# Revit family: Flooring_Entrance-Flooring_emco_MARSCHALL-Original
name_source: partatom
category: Furniture Systems
revit_build: Autodesk Revit 2018 (Build: 20190510_1515(x64)
units: mm (PartAtom-declared; Revit-internal decimal feet)

## family parameters
Cut with Voids When Loaded = No
Host = Face
OmniClass Number = 23.15.17.11.11
OmniClass Title = Floor Toppings
Part Type = Normal
Room Calculation Point = No
Round Connector Dimension = Use Diameter
Shared = No

## types (27) — shared parameters
Assembly Code = E2010400
Date Updated = 2023/08/22
Default Elevation = 1219 mm
Description = Rollable and hard-wearing original entrance mat with standard insert for supported installation options.
Keynote = 12480.A1
Manufacturer = Emco
Product data url = https://bimobject.com
Profile Material = Emco - Metal - Aluminium
Standard profile clearance approx. (mm) = 5 mm, rubber spacers
URL = https://www.emco-bau.com
Version = 1

## per-type parameters (varying)
- Large With ribbed carpet insert 512 SLR: Brush strip=No; Cassette brush=No; Colour fastness to artificial light ISO 105-B02=good 6; Colour fastness to rubbing ISO 105 X12=good 4; Colour fastness to water ISO 105 E01=good 5; EPIMID=99871; Flammability=Insert available on request (surcharge applicable) with fire classification Cfl-s1 according to EN 13501.; Height 12=Yes; Height 17=No; Height 22=No; Large=Yes; Model=Large With ribbed carpet insert 512 SLR; Normal=No; Pile material=100% PP (polypropylene); Profile width (mm)=46.5 mm; Scraping edge=No; Slip resistance=R 11 slip resistance as per DIN 51130; Tread surface=Recessed, robust, weather-proof, ribbed carpet strips.; Weight (kg/m2)=95; z_Height=12 mm  [stored 0.0393701 ft]; z_edge_height=16 mm  [stored 0.0524934 ft]; z_insert_offset=52 mm; z_insert_width=47 mm; z_slot_offest=49 mm  [stored 0.160761 ft]; z_slot_width=5 mm  [stored 0.0164042 ft]
- Large With ribbed carpet insert 517 SLR: Brush strip=No; Cassette brush=No; Colour fastness to artificial light ISO 105-B02=good 6; Colour fastness to rubbing ISO 105 X12=good 4; Colour fastness to water ISO 105 E01=good 5; EPIMID=99873; Flammability=Insert available on request (surcharge applicable) with fire classification Cfl-s1 according to EN 13501.; Height 12=No; Height 17=Yes; Height 22=No; Large=Yes; Model=Large With ribbed carpet insert 517 SLR; Normal=No; Pile material=100% PP (polypropylene); Profile width (mm)=46.5 mm; Scraping edge=No; Slip resistance=R 11 slip resistance as per DIN 51130; Tread surface=Recessed, robust, weather-proof, ribbed carpet strips.; Weight (kg/m2)=119; z_Height=17 mm; z_edge_height=20 mm  [stored 0.0656168 ft]; z_insert_offset=52 mm; z_insert_width=47 mm; z_slot_offest=49 mm  [stored 0.160761 ft]; z_slot_width=5 mm  [stored 0.0164042 ft]
- Large With ribbed carpet insert 522 SLR: Brush strip=No; Cassette brush=No; Colour fastness to artificial light ISO 105-B02=good 6; Colour fastness to rubbing ISO 105 X12=good 4; Colour fastness to water ISO 105 E01=good 5; EPIMID=99875; Flammability=Insert available on request (surcharge applicable) with fire classification Cfl-s1 according to EN 13501.; Height 12=No; Height 17=No; Height 22=Yes; Large=Yes; Model=Large With ribbed carpet insert 522 SLR; Normal=No; Pile material=100% PP (polypropylene); Profile width (mm)=46.5 mm; Scraping edge=No; Slip resistance=R 11 slip resistance as per DIN 51130; Tread surface=Recessed, robust, weather-proof, ribbed carpet strips.; Weight (kg/m2)=13.2; z_Height=22 mm  [stored 0.0721785 ft]; z_edge_height=25 mm  [stored 0.082021 ft]; z_insert_offset=52 mm; z_insert_width=47 mm; z_slot_offest=49 mm  [stored 0.160761 ft]; z_slot_width=5 mm  [stored 0.0164042 ft]
- Large With ribbed carpet insert and brush strip 517 SLRB: Brush strip=Yes; Cassette brush=No; Colour fastness to artificial light ISO 105-B02=good 6; Colour fastness to rubbing ISO 105 X12=good 4; Colour fastness to water ISO 105 E01=good 5; EPIMID=99939; Flammability=Insert available on request (surcharge applicable) with fire classification Cfl-s1 according to EN 13501.; Height 12=No; Height 17=Yes; Height 22=No; Large=Yes; Model=Large With ribbed carpet insert and brush strip 517 SLRB; Normal=No; Pile material=100% PP (polypropylene); Profile width (mm)=46.5 mm; Scraping edge=No; Slip resistance=-; Tread surface=Recessed, robust, weather-proof, ribbed carpet strips, also with brush strips mounted between the profiles.; Weight (kg/m2)=121; z_Height=17 mm; z_edge_height=20 mm  [stored 0.0656168 ft]; z_insert_offset=66 mm; z_insert_width=47 mm; z_slot_offest=56 mm; z_slot_width=20 mm  [stored 0.0656168 ft]
- Large With ribbed carpet insert and brush strip 522 SLRB: Brush strip=Yes; Cassette brush=No; Colour fastness to artificial light ISO 105-B02=good 6; Colour fastness to rubbing ISO 105 X12=good 4; Colour fastness to water ISO 105 E01=good 5; EPIMID=99941; Flammability=Insert available on request (surcharge applicable) with fire classification Cfl-s1 according to EN 13501.; Height 12=No; Height 17=No; Height 22=Yes; Large=Yes; Model=Large With ribbed carpet insert and brush strip 522 SLRB; Normal=No; Pile material=100% PP (polypropylene); Profile width (mm)=46.5 mm; Scraping edge=No; Slip resistance=-; Tread surface=Recessed, robust, weather-proof, ribbed carpet strips, also with brush strips mounted between the profiles.; Weight (kg/m2)=13.4; z_Height=22 mm  [stored 0.0721785 ft]; z_edge_height=25 mm  [stored 0.082021 ft]; z_insert_offset=66 mm; z_insert_width=47 mm; z_slot_offest=56 mm; z_slot_width=20 mm  [stored 0.0656168 ft]
- Large With ribbed carpet insert and scraper bar 512 SLRK: Brush strip=No; Cassette brush=No; Colour fastness to artificial light ISO 105-B02=good 6; Colour fastness to rubbing ISO 105 X12=good 4; Colour fastness to water ISO 105 E01=good 5; EPIMID=99944; Flammability=Insert available on request (surcharge applicable) with fire classification Cfl-s1 according to EN 13501.; Height 12=Yes; Height 17=No; Height 22=No; Large=Yes; Model=Large With ribbed carpet insert and scraper bar 512 SLRK; Normal=No; Pile material=100% PP (polypropylene); Profile width (mm)=46.5 mm; Scraping edge=Yes; Slip resistance=-; Tread surface=Recessed, robust, weather-proof, ribbed carpet strips, also with scraper bars mounted between the profiles.; Weight (kg/m2)=95; z_Height=12 mm  [stored 0.0393701 ft]; z_edge_height=16 mm  [stored 0.0524934 ft]; z_insert_offset=62 mm; z_insert_width=47 mm; z_slot_offest=54 mm; z_slot_width=15 mm  [stored 0.0492126 ft]
- Large With ribbed carpet insert and scraper bar 517 SLRK: Brush strip=No; Cassette brush=No; Colour fastness to artificial light ISO 105-B02=good 6; Colour fastness to rubbing ISO 105 X12=good 4; Colour fastness to water ISO 105 E01=good 5; EPIMID=99945; Flammability=Insert available on request (surcharge applicable) with fire classification Cfl-s1 according to EN 13501.; Height 12=No; Height 17=Yes; Height 22=No; Large=Yes; Model=Large With ribbed carpet insert and scraper bar 517 SLRK; Normal=No; Pile material=100% PP (polypropylene); Profile width (mm)=46.5 mm; Scraping edge=Yes; Slip resistance=-; Tread surface=Recessed, robust, weather-proof, ribbed carpet strips, also with scraper bars mounted between the profiles.; Weight (kg/m2)=12.3; z_Height=17 mm; z_edge_height=20 mm  [stored 0.0656168 ft]; z_insert_offset=62 mm; z_insert_width=47 mm; z_slot_offest=54 mm; z_slot_width=15 mm  [stored 0.0492126 ft]
- Large With ribbed carpet insert and scraper bar 522 SLRK: Brush strip=No; Cassette brush=No; Colour fastness to artificial light ISO 105-B02=good 6; Colour fastness to rubbing ISO 105 X12=good 4; Colour fastness to water ISO 105 E01=good 5; EPIMID=99947; Flammability=Insert available on request (surcharge applicable) with fire classification Cfl-s1 according to EN 13501.; Height 12=No; Height 17=No; Height 22=Yes; Large=Yes; Model=Large With ribbed carpet insert and scraper bar 522 SLRK; Normal=No; Pile material=100% PP (polypropylene); Profile width (mm)=46.5 mm; Scraping edge=Yes; Slip resistance=-; Tread surface=Recessed, robust, weather-proof, ribbed carpet strips, also with scraper bars mounted between the profiles.; Weight (kg/m2)=141; z_Height=22 mm  [stored 0.0721785 ft]; z_edge_height=25 mm  [stored 0.082021 ft]; z_insert_offset=62 mm; z_insert_width=47 mm; z_slot_offest=54 mm; z_slot_width=15 mm  [stored 0.0492126 ft]
- With cassette brush 512 SCB: Brush strip=No; Cassette brush=Yes; Colour fastness to artificial light ISO 105-B02=-; Colour fastness to rubbing ISO 105 X12=-; Colour fastness to water ISO 105 E01=-; EPIMID=99884; Flammability=Complete mat system (for bristle bundles in black) available on request (surcharge applicable) with fire classification Cfl-s1 according to EN 13501.; Height 12=Yes; Height 17=No; Height 22=No; Large=No; Model=With cassette brush 512 SCB; Normal=Yes; Pile material=-; Profile width (mm)=30 mm; Scraping edge=No; Slip resistance=R 13 slip resistance as per DIN 51130; Tread surface=Recessed, robust, weather-proof cassette sections, equipped with brush bundles arranged parallel to one another. Actual mat height: + 1 to 2 mm.; Weight (kg/m2)=167; z_Height=12 mm  [stored 0.0393701 ft]; z_edge_height=16 mm  [stored 0.0524934 ft]; z_insert_offset=35 mm; z_insert_width=30 mm  [stored 0.0984252 ft]; z_slot_offest=33 mm; z_slot_width=5 mm  [stored 0.0164042 ft]
- With cassette brush 517 SCB: Brush strip=No; Cassette brush=Yes; Colour fastness to artificial light ISO 105-B02=-; Colour fastness to rubbing ISO 105 X12=-; Colour fastness to water ISO 105 E01=-; EPIMID=99882; Flammability=Complete mat system (for bristle bundles in black) available on request (surcharge applicable) with fire classification Cfl-s1 according to EN 13501.; Height 12=No; Height 17=Yes; Height 22=No; Large=No; Model=With cassette brush 517 SCB; Normal=Yes; Pile material=-; Profile width (mm)=30 mm; Scraping edge=No; Slip resistance=R 13 slip resistance as per DIN 51130; Tread surface=Recessed, robust, weather-proof cassette sections, equipped with brush bundles arranged parallel to one another. Actual mat height: + 1 to 2 mm.; Weight (kg/m2)=194; z_Height=17 mm; z_edge_height=20 mm  [stored 0.0656168 ft]; z_insert_offset=35 mm; z_insert_width=30 mm  [stored 0.0984252 ft]; z_slot_offest=33 mm; z_slot_width=5 mm  [stored 0.0164042 ft]
- With cassette brush 522 SCB: Brush strip=No; Cassette brush=Yes; Colour fastness to artificial light ISO 105-B02=-; Colour fastness to rubbing ISO 105 X12=-; Colour fastness to water ISO 105 E01=-; EPIMID=99883; Flammability=Complete mat system (for bristle bundles in black) available on request (surcharge applicable) with fire classification Cfl-s1 according to EN 13501.; Height 12=No; Height 17=No; Height 22=Yes; Large=No; Model=With cassette brush 522 SCB; Normal=Yes; Pile material=-; Profile width (mm)=30 mm; Scraping edge=No; Slip resistance=R 13 slip resistance as per DIN 51130; Tread surface=Recessed, robust, weather-proof cassette sections, equipped with brush bundles arranged parallel to one another. Actual mat height: + 1 to 2 mm.; Weight (kg/m2)=215; z_Height=22 mm  [stored 0.0721785 ft]; z_edge_height=25 mm  [stored 0.082021 ft]; z_insert_offset=35 mm; z_insert_width=30 mm  [stored 0.0984252 ft]; z_slot_offest=33 mm; z_slot_width=5 mm  [stored 0.0164042 ft]
- With ribbed carpet insert 512 SR: Brush strip=No; Cassette brush=No; Colour fastness to artificial light ISO 105-B02=good 6; Colour fastness to rubbing ISO 105 X12=good 4; Colour fastness to water ISO 105 E01=good 5; EPIMID=99870; Flammability=Insert available on request (surcharge applicable) with fire classification Cfl-s1 according to EN 13501.; Height 12=Yes; Height 17=No; Height 22=No; Large=No; Model=With ribbed carpet insert 512 SR; Normal=Yes; Pile material=100% PP (polypropylene); Profile width (mm)=30 mm; Scraping edge=No; Slip resistance=R 11 slip resistance as per DIN 51130; Tread surface=Recessed, robust, weather-proof, ribbed carpet strips.; Weight (kg/m2)=11; z_Height=12 mm  [stored 0.0393701 ft]; z_edge_height=16 mm  [stored 0.0524934 ft]; z_insert_offset=35 mm; z_insert_width=30 mm  [stored 0.0984252 ft]; z_slot_offest=33 mm; z_slot_width=5 mm  [stored 0.0164042 ft]
- With ribbed carpet insert 517 SR: Brush strip=No; Cassette brush=No; Colour fastness to artificial light ISO 105-B02=good 6; Colour fastness to rubbing ISO 105 X12=good 4; Colour fastness to water ISO 105 E01=good 5; EPIMID=99872; Flammability=Insert available on request (surcharge applicable) with fire classification Cfl-s1 according to EN 13501.; Height 12=No; Height 17=Yes; Height 22=No; Large=No; Model=With ribbed carpet insert 517 SR; Normal=Yes; Pile material=100% PP (polypropylene); Profile width (mm)=30 mm; Scraping edge=No; Slip resistance=R 11 slip resistance as per DIN 51130; Tread surface=Recessed, robust, weather-proof, ribbed carpet strips.; Weight (kg/m2)=13.7; z_Height=17 mm; z_edge_height=20 mm  [stored 0.0656168 ft]; z_insert_offset=35 mm; z_insert_width=30 mm  [stored 0.0984252 ft]; z_slot_offest=33 mm; z_slot_width=5 mm  [stored 0.0164042 ft]
- With ribbed carpet insert 522 SR: Brush strip=No; Cassette brush=No; Colour fastness to artificial light ISO 105-B02=good 6; Colour fastness to rubbing ISO 105 X12=good 4; Colour fastness to water ISO 105 E01=good 5; EPIMID=99874; Flammability=Insert available on request (surcharge applicable) with fire classification Cfl-s1 according to EN 13501.; Height 12=No; Height 17=No; Height 22=Yes; Large=No; Model=With ribbed carpet insert 522 SR; Normal=Yes; Pile material=100% PP (polypropylene); Profile width (mm)=30 mm; Scraping edge=No; Slip resistance=R 11 slip resistance as per DIN 51130; Tread surface=Recessed, robust, weather-proof, ribbed carpet strips.; Weight (kg/m2)=14.7; z_Height=22 mm  [stored 0.0721785 ft]; z_edge_height=25 mm  [stored 0.082021 ft]; z_insert_offset=35 mm; z_insert_width=30 mm  [stored 0.0984252 ft]; z_slot_offest=33 mm; z_slot_width=5 mm  [stored 0.0164042 ft]
- With ribbed carpet insert and brush strip 517 SRB: Brush strip=Yes; Cassette brush=No; Colour fastness to artificial light ISO 105-B02=good 6; Colour fastness to rubbing ISO 105 X12=good 4; Colour fastness to water ISO 105 E01=good 5; EPIMID=99938; Flammability=Insert available on request (surcharge applicable) with fire classification Cfl-s1 according to EN 13501.; Height 12=No; Height 17=Yes; Height 22=No; Large=No; Model=With ribbed carpet insert and brush strip 517 SRB; Normal=Yes; Pile material=100% PP (polypropylene); Profile width (mm)=30 mm; Scraping edge=No; Slip resistance=-; Tread surface=Recessed, robust, weather-proof, ribbed carpet strips, also with brush strips mounted between the profiles.; Weight (kg/m2)=12.5; z_Height=17 mm; z_edge_height=20 mm  [stored 0.0656168 ft]; z_insert_offset=50 mm; z_insert_width=30 mm  [stored 0.0984252 ft]; z_slot_offest=40 mm  [stored 0.131234 ft]; z_slot_width=20 mm  [stored 0.0656168 ft]
- With ribbed carpet insert and brush strip 522 SRB: Brush strip=Yes; Cassette brush=No; Colour fastness to artificial light ISO 105-B02=good 6; Colour fastness to rubbing ISO 105 X12=good 4; Colour fastness to water ISO 105 E01=good 5; EPIMID=99940; Flammability=Insert available on request (surcharge applicable) with fire classification Cfl-s1 according to EN 13501.; Height 12=No; Height 17=No; Height 22=Yes; Large=No; Model=With ribbed carpet insert and brush strip 522 SRB; Normal=Yes; Pile material=100% PP (polypropylene); Profile width (mm)=30 mm; Scraping edge=No; Slip resistance=-; Tread surface=Recessed, robust, weather-proof, ribbed carpet strips, also with brush strips mounted between the profiles.; Weight (kg/m2)=14.3; z_Height=22 mm  [stored 0.0721785 ft]; z_edge_height=25 mm  [stored 0.082021 ft]; z_insert_offset=50 mm; z_insert_width=30 mm  [stored 0.0984252 ft]; z_slot_offest=40 mm  [stored 0.131234 ft]; z_slot_width=20 mm  [stored 0.0656168 ft]
- With ribbed carpet insert and scraper bar 512 SRK: Brush strip=No; Cassette brush=No; Colour fastness to artificial light ISO 105-B02=good 6; Colour fastness to rubbing ISO 105 X12=good 4; Colour fastness to water ISO 105 E01=good 5; EPIMID=99942; Flammability=Insert available on request (surcharge applicable) with fire classification Cfl-s1 according to EN 13501.; Height 12=Yes; Height 17=No; Height 22=No; Large=No; Model=With ribbed carpet insert and scraper bar 512 SRK; Normal=Yes; Pile material=100% PP (polypropylene); Profile width (mm)=30 mm; Scraping edge=Yes; Slip resistance=-; Tread surface=Recessed, robust, weather-proof, ribbed carpet strips, also with scraper bars mounted between the profiles.; Weight (kg/m2)=10.8; z_Height=12 mm  [stored 0.0393701 ft]; z_edge_height=16 mm  [stored 0.0524934 ft]; z_insert_offset=45 mm; z_insert_width=30 mm  [stored 0.0984252 ft]; z_slot_offest=38 mm; z_slot_width=15 mm  [stored 0.0492126 ft]
- With ribbed carpet insert and scraper bar 517 SRK: Brush strip=No; Cassette brush=No; Colour fastness to artificial light ISO 105-B02=good 6; Colour fastness to rubbing ISO 105 X12=good 4; Colour fastness to water ISO 105 E01=good 5; EPIMID=99943; Flammability=Insert available on request (surcharge applicable) with fire classification Cfl-s1 according to EN 13501.; Height 12=No; Height 17=Yes; Height 22=No; Large=No; Model=With ribbed carpet insert and scraper bar 517 SRK; Normal=Yes; Pile material=100% PP (polypropylene); Profile width (mm)=30 mm; Scraping edge=Yes; Slip resistance=-; Tread surface=Recessed, robust, weather-proof, ribbed carpet strips, also with scraper bars mounted between the profiles.; Weight (kg/m2)=13.4; z_Height=17 mm; z_edge_height=20 mm  [stored 0.0656168 ft]; z_insert_offset=45 mm; z_insert_width=30 mm  [stored 0.0984252 ft]; z_slot_offest=38 mm; z_slot_width=15 mm  [stored 0.0492126 ft]
- With ribbed carpet insert and scraper bar 522 SRK: Brush strip=No; Cassette brush=No; Colour fastness to artificial light ISO 105-B02=good 6; Colour fastness to rubbing ISO 105 X12=good 4; Colour fastness to water ISO 105 E01=good 5; EPIMID=99946; Flammability=Insert available on request (surcharge applicable) with fire classification Cfl-s1 according to EN 13501.; Height 12=No; Height 17=No; Height 22=Yes; Large=No; Model=With ribbed carpet insert and scraper bar 522 SRK; Normal=Yes; Pile material=100% PP (polypropylene); Profile width (mm)=30 mm; Scraping edge=Yes; Slip resistance=-; Tread surface=Recessed, robust, weather-proof, ribbed carpet strips, also with scraper bars mounted between the profiles.; Weight (kg/m2)=16; z_Height=22 mm  [stored 0.0721785 ft]; z_edge_height=25 mm  [stored 0.082021 ft]; z_insert_offset=45 mm; z_insert_width=30 mm  [stored 0.0984252 ft]; z_slot_offest=38 mm; z_slot_width=15 mm  [stored 0.0492126 ft]
- With rubber insert 512 SG: Brush strip=No; Cassette brush=No; Colour fastness to artificial light ISO 105-B02=-; Colour fastness to rubbing ISO 105 X12=-; Colour fastness to water ISO 105 E01=-; EPIMID=99879; Flammability=Complete mat system available on request (surcharge applicable) with fire classification Bfl-s1 according to EN 13501.; Height 12=Yes; Height 17=No; Height 22=No; Large=No; Model=With rubber insert 512 SG; Normal=Yes; Pile material=-; Profile width (mm)=30 mm; Scraping edge=No; Slip resistance=R 9 slip resistance as per DIN 51130; Tread surface=Recessed, robust, weather-proof profiled rubber inserts.; Weight (kg/m2)=15.5; z_Height=12 mm  [stored 0.0393701 ft]; z_edge_height=16 mm  [stored 0.0524934 ft]; z_insert_offset=35 mm; z_insert_width=30 mm  [stored 0.0984252 ft]; z_slot_offest=33 mm; z_slot_width=5 mm  [stored 0.0164042 ft]
- With rubber insert 512 SGK: Brush strip=No; Cassette brush=No; Colour fastness to artificial light ISO 105-B02=-; Colour fastness to rubbing ISO 105 X12=-; Colour fastness to water ISO 105 E01=-; EPIMID=99877; Flammability=Complete mat system available on request (surcharge applicable) with fire classification Bfl-s1 according to EN 13501.; Height 12=No; Height 17=Yes; Height 22=No; Large=No; Model=With rubber insert 517 SG; Normal=Yes; Pile material=-; Profile width (mm)=30 mm; Scraping edge=No; Slip resistance=R 9 slip resistance as per DIN 51130; Tread surface=Recessed, robust, weather-proof profiled rubber inserts.; Weight (kg/m2)=18.2; z_Height=17 mm; z_edge_height=20 mm  [stored 0.0656168 ft]; z_insert_offset=35 mm; z_insert_width=30 mm  [stored 0.0984252 ft]; z_slot_offest=33 mm; z_slot_width=5 mm  [stored 0.0164042 ft]
- With rubber insert 517 SG: Brush strip=No; Cassette brush=No; Colour fastness to artificial light ISO 105-B02=-; Colour fastness to rubbing ISO 105 X12=-; Colour fastness to water ISO 105 E01=-; EPIMID=99878; Flammability=Complete mat system available on request (surcharge applicable) with fire classification Bfl-s1 according to EN 13501.; Height 12=No; Height 17=No; Height 22=Yes; Large=No; Model=With rubber insert 522 SG; Normal=Yes; Pile material=-; Profile width (mm)=30 mm; Scraping edge=No; Slip resistance=R 9 slip resistance as per DIN 51130; Tread surface=Recessed, robust, weather-proof profiled rubber inserts.; Weight (kg/m2)=20.3; z_Height=22 mm  [stored 0.0721785 ft]; z_edge_height=25 mm  [stored 0.082021 ft]; z_insert_offset=35 mm; z_insert_width=30 mm  [stored 0.0984252 ft]; z_slot_offest=33 mm; z_slot_width=5 mm  [stored 0.0164042 ft]
- With rubber insert 517 SGB: Brush strip=Yes; Cassette brush=No; Colour fastness to artificial light ISO 105-B02=-; Colour fastness to rubbing ISO 105 X12=-; Colour fastness to water ISO 105 E01=-; EPIMID=105767; Flammability=Insert available on request (surcharge applicable) with fire classification Bfl-s1 according to EN 13501.; Height 12=No; Height 17=Yes; Height 22=No; Large=No; Model=With rubber insert and brush strip 517 SGB; Normal=Yes; Pile material=-; Profile width (mm)=30 mm; Scraping edge=No; Slip resistance=-; Tread surface=Recessed, robust, weather-proof profiled rubber inserts.; Weight (kg/m2)=15.7; z_Height=17 mm; z_edge_height=20 mm  [stored 0.0656168 ft]; z_insert_offset=50 mm; z_insert_width=30 mm  [stored 0.0984252 ft]; z_slot_offest=40 mm  [stored 0.131234 ft]; z_slot_width=20 mm  [stored 0.0656168 ft]
- With rubber insert 517 SGK: Brush strip=Yes; Cassette brush=No; Colour fastness to artificial light ISO 105-B02=-; Colour fastness to rubbing ISO 105 X12=-; Colour fastness to water ISO 105 E01=-; EPIMID=105768; Flammability=Insert available on request (surcharge applicable) with fire classification Bfl-s1 according to EN 13501.; Height 12=No; Height 17=No; Height 22=Yes; Large=No; Model=With rubber insert and brush strip 522 SGB; Normal=Yes; Pile material=-; Profile width (mm)=30 mm; Scraping edge=No; Slip resistance=-; Tread surface=Recessed, robust, weather-proof profiled rubber inserts.; Weight (kg/m2)=176; z_Height=22 mm  [stored 0.0721785 ft]; z_edge_height=25 mm  [stored 0.082021 ft]; z_insert_offset=50 mm; z_insert_width=30 mm  [stored 0.0984252 ft]; z_slot_offest=40 mm  [stored 0.131234 ft]; z_slot_width=20 mm  [stored 0.0656168 ft]
- With rubber insert 522 SG: Brush strip=No; Cassette brush=No; Colour fastness to artificial light ISO 105-B02=-; Colour fastness to rubbing ISO 105 X12=-; Colour fastness to water ISO 105 E01=-; EPIMID=105764; Flammability=Complete mat system available with fire classification Cfl-s1 in accordance with EN 13501 (tested by the Textiles & Flooring Institute GmbH).; Height 12=Yes; Height 17=No; Height 22=No; Large=No; Model=With rubber insert and scraper bar 512 SGK; Normal=Yes; Pile material=-; Profile width (mm)=30 mm; Scraping edge=Yes; Slip resistance=-; Tread surface=Recessed, robust, weather-proof profiled rubber inserts.; Weight (kg/m2)=142; z_Height=12 mm  [stored 0.0393701 ft]; z_edge_height=16 mm  [stored 0.0524934 ft]; z_insert_offset=45 mm; z_insert_width=30 mm  [stored 0.0984252 ft]; z_slot_offest=38 mm; z_slot_width=15 mm  [stored 0.0492126 ft]
- With rubber insert 522 SGB: Brush strip=No; Cassette brush=No; Colour fastness to artificial light ISO 105-B02=-; Colour fastness to rubbing ISO 105 X12=-; Colour fastness to water ISO 105 E01=-; EPIMID=105765; Flammability=Complete mat system available with fire classification Cfl-s1 in accordance with EN 13501 (tested by the Textiles & Flooring Institute GmbH).; Height 12=No; Height 17=Yes; Height 22=No; Large=No; Model=With rubber insert and scraper bar 517 SGK; Normal=Yes; Pile material=-; Profile width (mm)=30 mm; Scraping edge=Yes; Slip resistance=-; Tread surface=Recessed, robust, weather-proof profiled rubber inserts.; Weight (kg/m2)=167; z_Height=17 mm; z_edge_height=20 mm  [stored 0.0656168 ft]; z_insert_offset=45 mm; z_insert_width=30 mm  [stored 0.0984252 ft]; z_slot_offest=38 mm; z_slot_width=15 mm  [stored 0.0492126 ft]
- With rubber insert 522 SGK: Brush strip=No; Cassette brush=No; Colour fastness to artificial light ISO 105-B02=-; Colour fastness to rubbing ISO 105 X12=-; Colour fastness to water ISO 105 E01=-; EPIMID=105766; Flammability=Complete mat system available with fire classification Cfl-s1 in accordance with EN 13501 (tested by the Textiles & Flooring Institute GmbH).; Height 12=No; Height 17=No; Height 22=Yes; Large=No; Model=With rubber insert and scraper bar 522 SGK; Normal=Yes; Pile material=-; Profile width (mm)=30 mm; Scraping edge=Yes; Slip resistance=-; Tread surface=Recessed, robust, weather-proof profiled rubber inserts.; Weight (kg/m2)=194; z_Height=22 mm  [stored 0.0721785 ft]; z_edge_height=25 mm  [stored 0.082021 ft]; z_insert_offset=45 mm; z_insert_width=30 mm  [stored 0.0984252 ft]; z_slot_offest=38 mm; z_slot_width=15 mm  [stored 0.0492126 ft]

note: [stored X ft] marks values corroborated as IEEE doubles in the binary element streams (Revit-internal decimal feet)

## geometry (parser evidence)
native form markers: Sweep x9
no freeform markers — native parametric forms only
